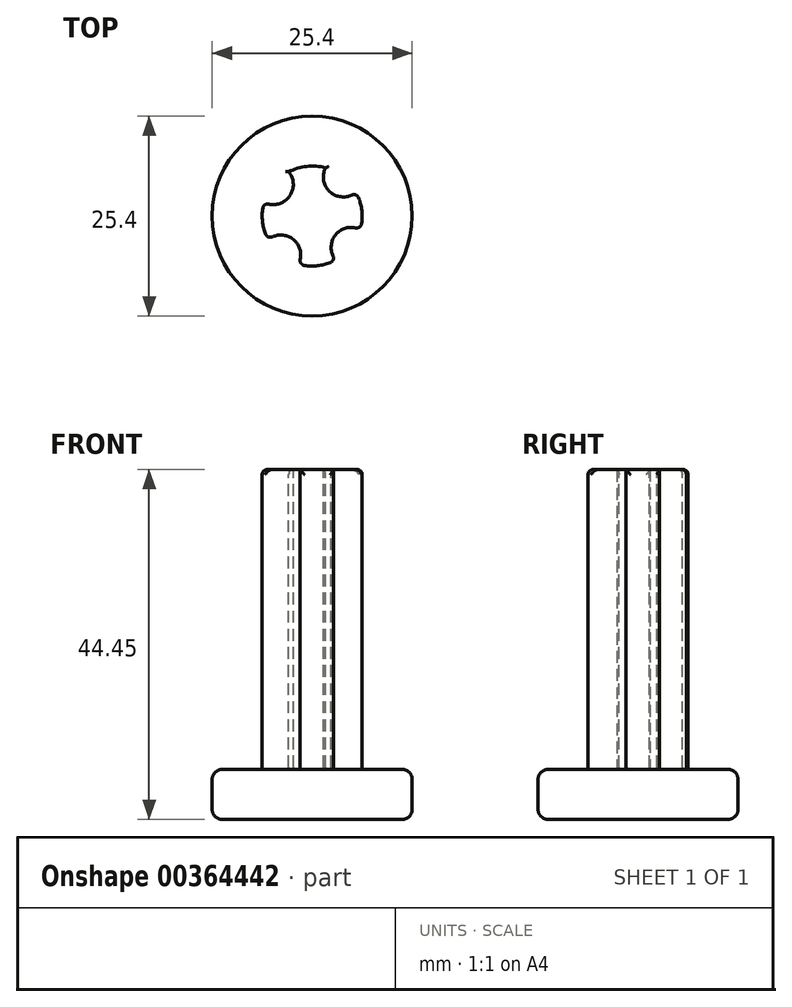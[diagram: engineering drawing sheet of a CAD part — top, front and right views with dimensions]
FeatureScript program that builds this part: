
annotation { "Feature Type Name" : "Feature", "Feature Type Description" : "" }
export const myFeature = defineFeature(function(context is Context, id is Id, definition is map)
    precondition{}
    {
        {
            var Q0;
            Q0=qCreatedBy(makeId("Top.planeOp"),FACE);
            var sketch = newSketch(context, id + "F0", { "sketchPlane" : qUnion([Q0])});
            skCircle(sketch, "E0", {"center": v(0, 0) * mm, "radius": 12.7 * mm});
            skSolve(sketch);
        }
        {
            var Q0;
            Q0 = qSketchRegion(id + "F0", true);
            extrude(context, id + "F1", {"entities" : qUnion([Q0]), "depth" : 6.35 * mm});
        }
        {
            var Q0;
            Q0=makeQuery(id+"F1.opExtrude","CAP_FACE",FACE,{"disambiguationData":[OSD([sQuery(id+"F0.wireOp",EDGE,"E0")])],"isStart":false});
            var sketch = newSketch(context, id + "F2", { "sketchPlane" : qUnion([Q0])});
            skCircle(sketch, "E1", {"center": v(0, 0) * mm, "radius": 6.35 * mm});
            skSolve(sketch);
        }
        {
            var Q0;
            Q0 = qSketchRegion(id + "F2", true);
            extrude(context, id + "F3", {"entities" : qUnion([Q0]), "operationType" : NewBodyOperationType.ADD, "depth" : 38.1 * mm});
        }
        {
            var Q0;
            Q0=makeQuery(id+"F3.opExtrude","CAP_FACE",FACE,{"disambiguationData":[OSD([sQuery(id+"F2.wireOp",EDGE,"E1")])],"isStart":false});
            var sketch = newSketch(context, id + "F4", { "sketchPlane" : qUnion([Q0])});
            skCircle(sketch, "E2", {"center": v(-3.99, -4.94) * mm, "radius": 2.54 * mm});
            skCircle(sketch, "E3", {"center": v(3.96, 4.97) * mm, "radius": 2.54 * mm});
            skCircle(sketch, "E4", {"center": v(-4.93, 4) * mm, "radius": 2.54 * mm});
            skCircle(sketch, "E5", {"center": v(4.95, -3.97) * mm, "radius": 2.54 * mm});
            skSolve(sketch);
        }
        {
            var Q0;
            {var subQ0=sQuery(id+"F4.wireOp",EDGE,"E3");var subQ1=makeQuery(id+"F3.opExtrude","CAP_EDGE",EDGE,{"disambiguationData":[OSD([sQuery(id+"F2.wireOp",EDGE,"E1")])],"isStart":false});var subQ2=makeQuery(id+"F4.imprint","INTERSECT",VERTEX,{"disambiguationData":[OD(0.0)],"derivedFrom":[subQ1,subQ0]});Q0=makeQuery(id+"F4.imprint","IMPRINT",FACE,{"disambiguationData":[TD([[makeQuery(id+"F4.imprint","IMPRINT",EDGE,{"disambiguationData":[TD([[subQ2,-1.0]])],"derivedFrom":subQ0}),1.0]])]});}
            var Q1;
            {var subQ0=sQuery(id+"F4.wireOp",EDGE,"E4");var subQ1=makeQuery(id+"F3.opExtrude","CAP_EDGE",EDGE,{"disambiguationData":[OSD([sQuery(id+"F2.wireOp",EDGE,"E1")])],"isStart":false});var subQ2=makeQuery(id+"F4.imprint","INTERSECT",VERTEX,{"disambiguationData":[OD(0.0)],"derivedFrom":[subQ1,subQ0]});Q1=makeQuery(id+"F4.imprint","IMPRINT",FACE,{"disambiguationData":[TD([[makeQuery(id+"F4.imprint","IMPRINT",EDGE,{"disambiguationData":[TD([[subQ2,-1.0]])],"derivedFrom":subQ0}),1.0]])]});}
            var Q2;
            {var subQ0=sQuery(id+"F4.wireOp",EDGE,"E2");var subQ1=makeQuery(id+"F3.opExtrude","CAP_EDGE",EDGE,{"disambiguationData":[OSD([sQuery(id+"F2.wireOp",EDGE,"E1")])],"isStart":false});var subQ2=makeQuery(id+"F4.imprint","INTERSECT",VERTEX,{"disambiguationData":[OD(0.0)],"derivedFrom":[subQ1,subQ0]});Q2=makeQuery(id+"F4.imprint","IMPRINT",FACE,{"disambiguationData":[TD([[makeQuery(id+"F4.imprint","IMPRINT",EDGE,{"disambiguationData":[TD([[subQ2,1.0]])],"derivedFrom":subQ0}),1.0]])]});}
            var Q3;
            {var subQ0=sQuery(id+"F4.wireOp",EDGE,"E5");var subQ1=makeQuery(id+"F3.opExtrude","CAP_EDGE",EDGE,{"disambiguationData":[OSD([sQuery(id+"F2.wireOp",EDGE,"E1")])],"isStart":false});var subQ2=makeQuery(id+"F4.imprint","INTERSECT",VERTEX,{"disambiguationData":[OD(0.0)],"derivedFrom":[subQ1,subQ0]});Q3=makeQuery(id+"F4.imprint","IMPRINT",FACE,{"disambiguationData":[TD([[makeQuery(id+"F4.imprint","IMPRINT",EDGE,{"disambiguationData":[TD([[subQ2,1.0]])],"derivedFrom":subQ0}),1.0]])]});}
            extrude(context, id + "F5", {"entities" : qUnion([Q0, Q1, Q2, Q3]), "operationType" : NewBodyOperationType.REMOVE, "oppositeDirection" : true, "depth" : 38.1 * mm});
        }
        {
            var Q0;
            Q0=makeQuery(id+"F5.boolean.opBoolean","COPY",EDGE,{"derivedFrom":makeQuery(id+"F5.opExtrude","CAP_EDGE",EDGE,{"disambiguationData":[OSD([sQuery(id+"F4.wireOp",EDGE,"E5")])],"isStart":true})});
            var Q1;
            Q1=makeQuery(id+"F5.boolean.opBoolean","COPY",EDGE,{"derivedFrom":makeQuery(id+"F5.opExtrude","CAP_EDGE",EDGE,{"disambiguationData":[OSD([sQuery(id+"F4.wireOp",EDGE,"E4")])],"isStart":true})});
            var Q2;
            {var subQ0=sQuery(id+"F2.wireOp",EDGE,"E1");Q2=makeQuery(id+"F5.boolean.opBoolean","SPLIT",EDGE,{"disambiguationData":[TD([makeQuery(id+"F3.opExtrude","SWEPT_FACE",FACE,{"disambiguationData":[OSD([subQ0])]}),makeQuery(id+"F3.opExtrude","CAP_FACE",FACE,{"disambiguationData":[OSD([subQ0])],"isStart":false}),makeQuery(id+"F5.opExtrude","SWEPT_FACE",FACE,{"disambiguationData":[OSD([sQuery(id+"F4.wireOp",EDGE,"E3")])]}),makeQuery(id+"F5.opExtrude","SWEPT_FACE",FACE,{"disambiguationData":[OSD([sQuery(id+"F4.wireOp",EDGE,"E4")])]})])],"derivedFrom":makeQuery(id+"F3.opExtrude","CAP_EDGE",EDGE,{"disambiguationData":[OSD([subQ0])],"isStart":false})});}
            var Q3;
            Q3=makeQuery(id+"F5.boolean.opBoolean","COPY",EDGE,{"derivedFrom":makeQuery(id+"F5.opExtrude","CAP_EDGE",EDGE,{"disambiguationData":[OSD([sQuery(id+"F4.wireOp",EDGE,"E3")])],"isStart":true})});
            var Q4;
            {var subQ0=sQuery(id+"F2.wireOp",EDGE,"E1");Q4=makeQuery(id+"F5.boolean.opBoolean","SPLIT",EDGE,{"disambiguationData":[TD([makeQuery(id+"F3.opExtrude","SWEPT_FACE",FACE,{"disambiguationData":[OSD([subQ0])]}),makeQuery(id+"F3.opExtrude","CAP_FACE",FACE,{"disambiguationData":[OSD([subQ0])],"isStart":false}),makeQuery(id+"F5.opExtrude","SWEPT_FACE",FACE,{"disambiguationData":[OSD([sQuery(id+"F4.wireOp",EDGE,"E3")])]}),makeQuery(id+"F5.opExtrude","SWEPT_FACE",FACE,{"disambiguationData":[OSD([sQuery(id+"F4.wireOp",EDGE,"E5")])]})])],"derivedFrom":makeQuery(id+"F3.opExtrude","CAP_EDGE",EDGE,{"disambiguationData":[OSD([subQ0])],"isStart":false})});}
            var Q5;
            {var subQ0=sQuery(id+"F2.wireOp",EDGE,"E1");Q5=makeQuery(id+"F5.boolean.opBoolean","SPLIT",EDGE,{"disambiguationData":[TD([makeQuery(id+"F3.opExtrude","SWEPT_FACE",FACE,{"disambiguationData":[OSD([subQ0])]}),makeQuery(id+"F3.opExtrude","CAP_FACE",FACE,{"disambiguationData":[OSD([subQ0])],"isStart":false}),makeQuery(id+"F5.opExtrude","SWEPT_FACE",FACE,{"disambiguationData":[OSD([sQuery(id+"F4.wireOp",EDGE,"E2")])]}),makeQuery(id+"F5.opExtrude","SWEPT_FACE",FACE,{"disambiguationData":[OSD([sQuery(id+"F4.wireOp",EDGE,"E5")])]})])],"derivedFrom":makeQuery(id+"F3.opExtrude","CAP_EDGE",EDGE,{"disambiguationData":[OSD([subQ0])],"isStart":false})});}
            var Q6;
            Q6=makeQuery(id+"F5.boolean.opBoolean","COPY",EDGE,{"derivedFrom":makeQuery(id+"F5.opExtrude","CAP_EDGE",EDGE,{"disambiguationData":[OSD([sQuery(id+"F4.wireOp",EDGE,"E2")])],"isStart":true})});
            var Q7;
            {var subQ0=sQuery(id+"F2.wireOp",EDGE,"E1");Q7=makeQuery(id+"F5.boolean.opBoolean","SPLIT",EDGE,{"disambiguationData":[TD([makeQuery(id+"F3.opExtrude","SWEPT_FACE",FACE,{"disambiguationData":[OSD([subQ0])]}),makeQuery(id+"F3.opExtrude","CAP_FACE",FACE,{"disambiguationData":[OSD([subQ0])],"isStart":false}),makeQuery(id+"F5.opExtrude","SWEPT_FACE",FACE,{"disambiguationData":[OSD([sQuery(id+"F4.wireOp",EDGE,"E2")])]}),makeQuery(id+"F5.opExtrude","SWEPT_FACE",FACE,{"disambiguationData":[OSD([sQuery(id+"F4.wireOp",EDGE,"E4")])]})])],"derivedFrom":makeQuery(id+"F3.opExtrude","CAP_EDGE",EDGE,{"disambiguationData":[OSD([subQ0])],"isStart":false})});}
            var Q8;
            {var subQ0=sQuery(id+"F4.wireOp",EDGE,"E5");var subQ1=sQuery(id+"F2.wireOp",EDGE,"E1");Q8=makeQuery(id+"F5.boolean.opBoolean","COPY",EDGE,{"derivedFrom":makeQuery(id+"F5.opExtrude","SWEPT_EDGE",EDGE,{"disambiguationData":[OSD([subQ1,subQ0]),TDD([makeQuery(id+"F4.imprint","INTERSECT",VERTEX,{"disambiguationData":[OD(0.0)],"derivedFrom":[makeQuery(id+"F3.opExtrude","CAP_EDGE",EDGE,{"disambiguationData":[OSD([subQ1])],"isStart":false}),subQ0]})])]})});}
            var Q9;
            {var subQ0=sQuery(id+"F4.wireOp",EDGE,"E5");var subQ1=sQuery(id+"F2.wireOp",EDGE,"E1");Q9=makeQuery(id+"F5.boolean.opBoolean","COPY",EDGE,{"derivedFrom":makeQuery(id+"F5.opExtrude","SWEPT_EDGE",EDGE,{"disambiguationData":[OSD([subQ1,subQ0]),TDD([makeQuery(id+"F4.imprint","INTERSECT",VERTEX,{"disambiguationData":[OD(1.0)],"derivedFrom":[makeQuery(id+"F3.opExtrude","CAP_EDGE",EDGE,{"disambiguationData":[OSD([subQ1])],"isStart":false}),subQ0]})])]})});}
            var Q10;
            {var subQ0=sQuery(id+"F4.wireOp",EDGE,"E3");var subQ1=sQuery(id+"F2.wireOp",EDGE,"E1");Q10=makeQuery(id+"F5.boolean.opBoolean","COPY",EDGE,{"derivedFrom":makeQuery(id+"F5.opExtrude","SWEPT_EDGE",EDGE,{"disambiguationData":[OSD([subQ1,subQ0]),TDD([makeQuery(id+"F4.imprint","INTERSECT",VERTEX,{"disambiguationData":[OD(1.0)],"derivedFrom":[makeQuery(id+"F3.opExtrude","CAP_EDGE",EDGE,{"disambiguationData":[OSD([subQ1])],"isStart":false}),subQ0]})])]})});}
            var Q11;
            {var subQ0=sQuery(id+"F4.wireOp",EDGE,"E3");var subQ1=sQuery(id+"F2.wireOp",EDGE,"E1");Q11=makeQuery(id+"F5.boolean.opBoolean","COPY",EDGE,{"derivedFrom":makeQuery(id+"F5.opExtrude","SWEPT_EDGE",EDGE,{"disambiguationData":[OSD([subQ1,subQ0]),TDD([makeQuery(id+"F4.imprint","INTERSECT",VERTEX,{"disambiguationData":[OD(0.0)],"derivedFrom":[makeQuery(id+"F3.opExtrude","CAP_EDGE",EDGE,{"disambiguationData":[OSD([subQ1])],"isStart":false}),subQ0]})])]})});}
            var Q12;
            {var subQ0=sQuery(id+"F4.wireOp",EDGE,"E4");var subQ1=sQuery(id+"F2.wireOp",EDGE,"E1");Q12=makeQuery(id+"F5.boolean.opBoolean","COPY",EDGE,{"derivedFrom":makeQuery(id+"F5.opExtrude","SWEPT_EDGE",EDGE,{"disambiguationData":[OSD([subQ1,subQ0]),TDD([makeQuery(id+"F4.imprint","INTERSECT",VERTEX,{"disambiguationData":[OD(1.0)],"derivedFrom":[makeQuery(id+"F3.opExtrude","CAP_EDGE",EDGE,{"disambiguationData":[OSD([subQ1])],"isStart":false}),subQ0]})])]})});}
            var Q13;
            {var subQ0=sQuery(id+"F4.wireOp",EDGE,"E4");var subQ1=sQuery(id+"F2.wireOp",EDGE,"E1");Q13=makeQuery(id+"F5.boolean.opBoolean","COPY",EDGE,{"derivedFrom":makeQuery(id+"F5.opExtrude","SWEPT_EDGE",EDGE,{"disambiguationData":[OSD([subQ1,subQ0]),TDD([makeQuery(id+"F4.imprint","INTERSECT",VERTEX,{"disambiguationData":[OD(0.0)],"derivedFrom":[makeQuery(id+"F3.opExtrude","CAP_EDGE",EDGE,{"disambiguationData":[OSD([subQ1])],"isStart":false}),subQ0]})])]})});}
            var Q14;
            {var subQ0=sQuery(id+"F4.wireOp",EDGE,"E2");var subQ1=sQuery(id+"F2.wireOp",EDGE,"E1");Q14=makeQuery(id+"F5.boolean.opBoolean","COPY",EDGE,{"derivedFrom":makeQuery(id+"F5.opExtrude","SWEPT_EDGE",EDGE,{"disambiguationData":[OSD([subQ1,subQ0]),TDD([makeQuery(id+"F4.imprint","INTERSECT",VERTEX,{"disambiguationData":[OD(0.0)],"derivedFrom":[makeQuery(id+"F3.opExtrude","CAP_EDGE",EDGE,{"disambiguationData":[OSD([subQ1])],"isStart":false}),subQ0]})])]})});}
            var Q15;
            {var subQ0=sQuery(id+"F4.wireOp",EDGE,"E2");var subQ1=sQuery(id+"F2.wireOp",EDGE,"E1");Q15=makeQuery(id+"F5.boolean.opBoolean","COPY",EDGE,{"derivedFrom":makeQuery(id+"F5.opExtrude","SWEPT_EDGE",EDGE,{"disambiguationData":[OSD([subQ1,subQ0]),TDD([makeQuery(id+"F4.imprint","INTERSECT",VERTEX,{"disambiguationData":[OD(1.0)],"derivedFrom":[makeQuery(id+"F3.opExtrude","CAP_EDGE",EDGE,{"disambiguationData":[OSD([subQ1])],"isStart":false}),subQ0]})])]})});}
            fillet(context, id + "F6", {"entities" : qUnion([Q0, Q1, Q2, Q3, Q4, Q5, Q6, Q7, Q8, Q9, Q10, Q11, Q12, Q13, Q14, Q15]), "radius" : 0.64 * mm, "tangentPropagation" : true, "allowEdgeOverflow" : false});
        }
        {
            var Q0;
            Q0=makeQuery(id+"F1.opExtrude","CAP_EDGE",EDGE,{"disambiguationData":[OSD([sQuery(id+"F0.wireOp",EDGE,"E0")])],"isStart":false});
            var Q1;
            Q1=makeQuery(id+"F1.opExtrude","CAP_EDGE",EDGE,{"disambiguationData":[OSD([sQuery(id+"F0.wireOp",EDGE,"E0")])],"isStart":true});
            fillet(context, id + "F7", {"entities" : qUnion([Q0, Q1]), "radius" : 1.27 * mm, "tangentPropagation" : true, "allowEdgeOverflow" : false});
        }
        {
            var Q0;
            {var subQ0=sQuery(id+"F2.wireOp",EDGE,"E1");Q0=makeQuery(id+"F5.boolean.opBoolean","MERGE",FACE,{"derivedFrom":[makeQuery(id+"F1.opExtrude","CAP_FACE",FACE,{"disambiguationData":[OSD([sQuery(id+"F0.wireOp",EDGE,"E0")])],"isStart":false}),makeQuery(id+"F5.opExtrude","CAP_FACE",FACE,{"disambiguationData":[OSD([subQ0,sQuery(id+"F4.wireOp",EDGE,"E2")])],"isStart":false}),makeQuery(id+"F5.opExtrude","CAP_FACE",FACE,{"disambiguationData":[OSD([subQ0,sQuery(id+"F4.wireOp",EDGE,"E3")])],"isStart":false}),makeQuery(id+"F5.opExtrude","CAP_FACE",FACE,{"disambiguationData":[OSD([subQ0,sQuery(id+"F4.wireOp",EDGE,"E4")])],"isStart":false}),makeQuery(id+"F5.opExtrude","CAP_FACE",FACE,{"disambiguationData":[OSD([subQ0,sQuery(id+"F4.wireOp",EDGE,"E5")])],"isStart":false})]});}
            fillet(context, id + "F8", {"entities" : qUnion([Q0]), "radius" : 0.25 * mm, "tangentPropagation" : true, "allowEdgeOverflow" : false});
        }
    });
